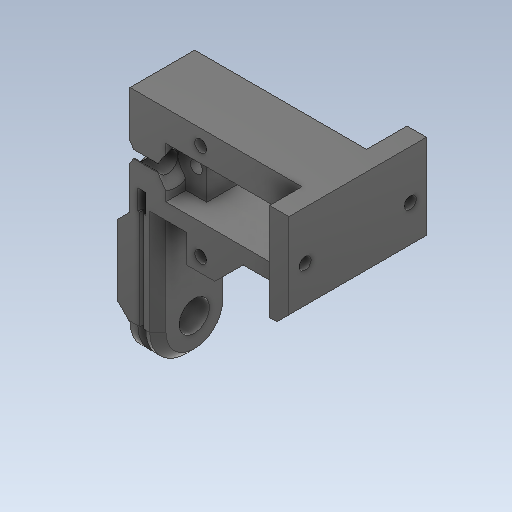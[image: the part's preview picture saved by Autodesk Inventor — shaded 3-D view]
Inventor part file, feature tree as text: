
AUTODESK INVENTOR PART (.ipt)
format: ipt  version: 2020 (Build 240168000, 168)  size: 464,896 bytes
history: native  units: in
note: dims shown in document units (in); Inventor stores cm internally (conversion verified against a paired STEP export)
features: sketch x35, other x3, plane x1
ambient origin geometry x8: Origin, YZ Plane, XZ Plane, XY Plane, X Axis, Y Axis, Z Axis, Center Point
bodies: Solid1 (feature_tree)
feature tree (39):
  other  "FermurSupport.ipt"
  other  "Solid1::FermurSupport.ipt"
  other  "TaggingFeature1"
  sketch  "Sketch1"  dims[d0=0.3937in]
  sketch  "Sketch2"
  sketch  "Sketch3"
  sketch  "Sketch4"
  sketch  "Sketch5"
  sketch  "Sketch6"
  sketch  "Sketch8"
  sketch  "Sketch10"
  sketch  "Sketch11"
  sketch  "Sketch12"
  sketch  "Sketch13"
  sketch  "Sketch14"
  sketch  "Sketch15"
  sketch  "Sketch17"
  sketch  "Sketch19"
  sketch  "Sketch21"
  sketch  "Sketch22"
  sketch  "Sketch23"
  sketch  "Sketch26"
  sketch  "Sketch27"
  sketch  "Sketch29"
  sketch  "Sketch32"
  sketch  "Sketch33"
  sketch  "Sketch36"
  sketch  "Sketch37"
  sketch  "Sketch38"
  sketch  "Sketch39"
  sketch  "Sketch41"
  sketch  "Sketch42"
  sketch  "Sketch43"
  sketch  "Sketch44"
  sketch  "Sketch45"
  sketch  "Sketch46"
  sketch  "Sketch47"
  sketch  "Sketch48"
  plane  "Work Plane1"
